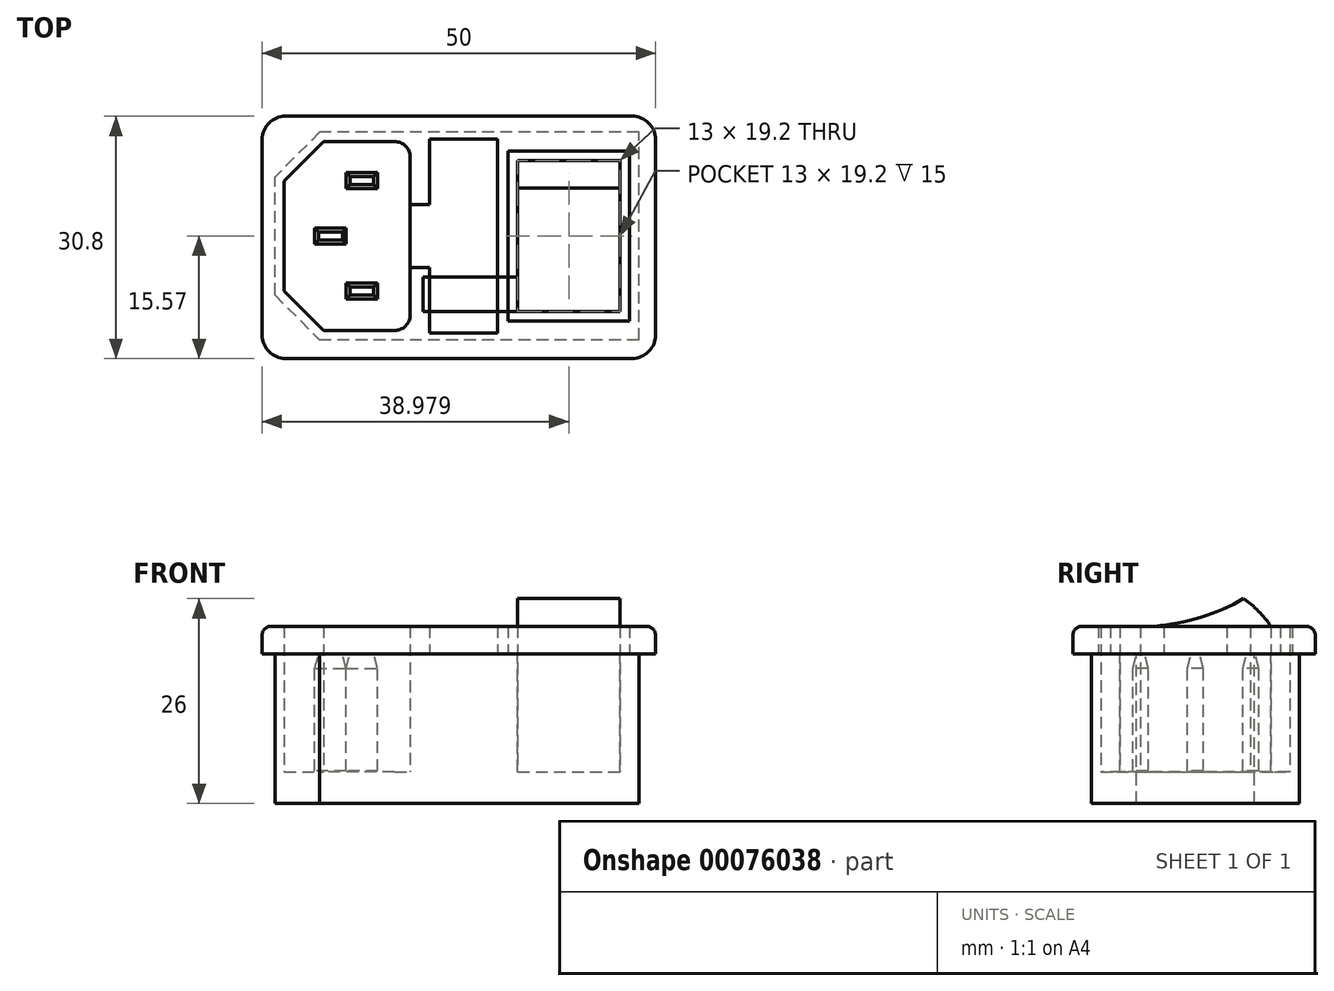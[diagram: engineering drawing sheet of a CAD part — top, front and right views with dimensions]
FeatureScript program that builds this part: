
annotation { "Feature Type Name" : "Feature", "Feature Type Description" : "" }
export const myFeature = defineFeature(function(context is Context, id is Id, definition is map)
    precondition{}
    {
        {
            var Q0;
            Q0=qCreatedBy(makeId("Top.planeOp"),FACE);
            var sketch = newSketch(context, id + "F0", { "sketchPlane" : qUnion([Q0])});
            skLineSegment(sketch, "E0.bottom", {"start": v(-22.59, 15.23) * mm, "end": v(21.41, 15.23) * mm});
            skLineSegment(sketch, "E0.top", {"start": v(-22.59, -15.57) * mm, "end": v(21.41, -15.57) * mm});
            skLineSegment(sketch, "E0.left", {"start": v(-25.59, 12.23) * mm, "end": v(-25.59, -12.57) * mm});
            skLineSegment(sketch, "E0.right", {"start": v(24.41, 12.23) * mm, "end": v(24.41, -12.57) * mm});
            skLineSegment(sketch, "E1.bottom", {"start": v(6.89, 9.6) * mm, "end": v(19.89, 9.6) * mm});
            skLineSegment(sketch, "E1.top", {"start": v(6.89, -9.6) * mm, "end": v(19.89, -9.6) * mm});
            skLineSegment(sketch, "E1.left", {"start": v(6.89, 9.6) * mm, "end": v(6.89, -9.6) * mm});
            skLineSegment(sketch, "E1.right", {"start": v(19.89, 9.6) * mm, "end": v(19.89, -9.6) * mm});
            skLineSegment(sketch, "E2.0", {"start": v(5.69, 10.8) * mm, "end": v(21.09, 10.8) * mm});
            skLineSegment(sketch, "E2.1", {"start": v(5.69, 10.8) * mm, "end": v(5.69, -10.8) * mm});
            skLineSegment(sketch, "E2.2", {"start": v(5.69, -10.8) * mm, "end": v(21.09, -10.8) * mm});
            skLineSegment(sketch, "E2.3", {"start": v(21.09, 10.8) * mm, "end": v(21.09, -10.8) * mm});
            skPoint(sketch, "E3", {"position": v(21.09, 0) * mm});
            skPoint(sketch, "E4", {"position": v(6.89, 0) * mm});
            skPoint(sketch, "E5", {"position": v(-0.59, -15.57) * mm});
            skPoint(sketch, "E6", {"position": v(-25.59, 0) * mm});
            skLineSegment(sketch, "E7.rect.bottom", {"start": v(-4.34, 12.33) * mm, "end": v(4.34, 12.33) * mm});
            skLineSegment(sketch, "E7.rect.top", {"start": v(-4.34, -12.33) * mm, "end": v(4.34, -12.33) * mm});
            skLineSegment(sketch, "E7.rect.left", {"start": v(-4.34, 12.33) * mm, "end": v(-4.34, -12.33) * mm});
            skLineSegment(sketch, "E7.rect.right", {"start": v(4.34, 12.33) * mm, "end": v(4.34, -12.33) * mm});
            skPoint(sketch, "E7.rect.middle", {"position": v(0, 0) * mm});
            skLineSegment(sketch, "E8.bottom", {"start": v(-8.76, -12) * mm, "end": v(-17.76, -12) * mm});
            skLineSegment(sketch, "E8.top", {"start": v(-8.76, 12) * mm, "end": v(-17.76, 12) * mm});
            skLineSegment(sketch, "E8.left", {"start": v(-6.76, -10) * mm, "end": v(-6.76, 10) * mm});
            skLineSegment(sketch, "E8.right", {"start": v(-22.76, -7) * mm, "end": v(-22.76, 7) * mm});
            skLineSegment(sketch, "E9", {"start": v(-17.76, 12) * mm, "end": v(-22.76, 7) * mm});
            skLineSegment(sketch, "E10", {"start": v(-22.76, -7) * mm, "end": v(-17.76, -12) * mm});
            skPoint(sketch, "E11", {"position": v(-6.76, 0) * mm});
            skPoint(sketch, "E12.visualSharp", {"position": v(24.41, 15.23) * mm});
            skArc(sketch, "E12.filletArc", {"start": v(24.41, 12.23) * mm, "mid": v(23.53, 14.35) * mm, "end": v(21.41, 15.23) * mm});
            skPoint(sketch, "E13.visualSharp", {"position": v(-25.59, 15.23) * mm});
            skArc(sketch, "E13.filletArc", {"start": v(-22.59, 15.23) * mm, "mid": v(-24.71, 14.35) * mm, "end": v(-25.59, 12.23) * mm});
            skPoint(sketch, "E14.visualSharp", {"position": v(-25.59, -15.57) * mm});
            skArc(sketch, "E14.filletArc", {"start": v(-25.59, -12.57) * mm, "mid": v(-24.71, -14.69) * mm, "end": v(-22.59, -15.57) * mm});
            skPoint(sketch, "E15.visualSharp", {"position": v(24.41, -15.57) * mm});
            skArc(sketch, "E15.filletArc", {"start": v(21.41, -15.57) * mm, "mid": v(23.53, -14.69) * mm, "end": v(24.41, -12.57) * mm});
            skPoint(sketch, "E16.visualSharp", {"position": v(-6.76, 12) * mm});
            skArc(sketch, "E16.filletArc", {"start": v(-6.76, 10) * mm, "mid": v(-7.34, 11.41) * mm, "end": v(-8.76, 12) * mm});
            skPoint(sketch, "E17.visualSharp", {"position": v(-6.76, -12) * mm});
            skArc(sketch, "E17.filletArc", {"start": v(-8.76, -12) * mm, "mid": v(-7.34, -11.41) * mm, "end": v(-6.76, -10) * mm});
            skLineSegment(sketch, "E18.rect.bottom", {"start": v(-14.89, 1) * mm, "end": v(-18.89, 1) * mm});
            skLineSegment(sketch, "E18.rect.top", {"start": v(-14.89, -1) * mm, "end": v(-18.89, -1) * mm});
            skLineSegment(sketch, "E18.rect.left", {"start": v(-14.89, 1) * mm, "end": v(-14.89, -1) * mm});
            skLineSegment(sketch, "E18.rect.right", {"start": v(-18.89, 1) * mm, "end": v(-18.89, -1) * mm});
            skPoint(sketch, "E18.rect.middle", {"position": v(-16.89, 0) * mm});
            skPoint(sketch, "E18.rect.middle.positionSnap0", {"position": v(-4.34, 0) * mm});
            skPoint(sketch, "E18.rect.centerSnap0", {"position": v(-4.34, 0) * mm});
            skLineSegment(sketch, "E19.rect.bottom", {"start": v(-10.89, 8.05) * mm, "end": v(-14.89, 8.05) * mm});
            skLineSegment(sketch, "E19.rect.right", {"start": v(-14.89, 8.05) * mm, "end": v(-14.89, 6.05) * mm});
            skLineSegment(sketch, "E19.rect.top", {"start": v(-10.89, 6.05) * mm, "end": v(-14.89, 6.05) * mm});
            skLineSegment(sketch, "E19.rect.left", {"start": v(-10.89, 8.05) * mm, "end": v(-10.89, 6.05) * mm});
            skPoint(sketch, "E19.rect.middle", {"position": v(-12.89, 7.05) * mm});
            skLineSegment(sketch, "E20.rect.bottom", {"start": v(-10.89, -5.97) * mm, "end": v(-14.89, -5.97) * mm});
            skLineSegment(sketch, "E20.rect.right", {"start": v(-14.89, -5.97) * mm, "end": v(-14.89, -7.97) * mm});
            skLineSegment(sketch, "E20.rect.top", {"start": v(-10.89, -7.97) * mm, "end": v(-14.89, -7.97) * mm});
            skLineSegment(sketch, "E20.rect.left", {"start": v(-10.89, -5.97) * mm, "end": v(-10.89, -7.97) * mm});
            skPoint(sketch, "E20.rect.middle", {"position": v(-12.89, -6.97) * mm});
            skLineSegment(sketch, "E21", {"start": v(-19.34, -78.26) * mm, "end": v(-26.2, -78.26) * mm});
            skLineSegment(sketch, "E22", {"start": v(-20.2, -74.76) * mm, "end": v(-25.73, -74.76) * mm});
            skLineSegment(sketch, "E23", {"start": v(-19.89, -48.56) * mm, "end": v(-26.2, -48.56) * mm});
            skLineSegment(sketch, "E24.0", {"start": v(-8.76, 13.2) * mm, "end": v(-18.25, 13.2) * mm});
            skLineSegment(sketch, "E24.1", {"start": v(-8.76, -13.2) * mm, "end": v(-18.25, -13.2) * mm});
            skLineSegment(sketch, "E24.2", {"start": v(-23.96, -7.5) * mm, "end": v(-18.25, -13.2) * mm});
            skLineSegment(sketch, "E24.3", {"start": v(-23.96, -7.5) * mm, "end": v(-23.96, 7.5) * mm});
            skLineSegment(sketch, "E24.4", {"start": v(-18.25, 13.2) * mm, "end": v(-23.96, 7.5) * mm});
            skLineSegment(sketch, "E25", {"start": v(-8.76, -13.2) * mm, "end": v(22.29, -13.2) * mm});
            skLineSegment(sketch, "E26", {"start": v(22.29, -13.2) * mm, "end": v(22.29, 13.2) * mm});
            skLineSegment(sketch, "E27", {"start": v(22.29, 13.2) * mm, "end": v(-8.76, 13.2) * mm});
            skLineSegment(sketch, "E28", {"start": v(-6.76, 4) * mm, "end": v(-4.34, 4) * mm});
            skLineSegment(sketch, "E29", {"start": v(-6.76, -4) * mm, "end": v(-4.34, -4) * mm});
            skSolve(sketch);
        }
        {
            var Q0;
            Q0=makeQuery(id+"F0.imprint","IMPRINT",FACE,{"disambiguationData":[TD([[makeQuery(id+"F0.imprint","IMPRINT",EDGE,{"derivedFrom":sQuery(id+"F0.wireOp",EDGE,"E0.bottom")}),-1.0]])]});
            var Q1;
            Q1=makeQuery(id+"F0.imprint","IMPRINT",FACE,{"disambiguationData":[TD([[makeQuery(id+"F0.imprint","IMPRINT",EDGE,{"derivedFrom":sQuery(id+"F0.wireOp",EDGE,"E2.0")}),1.0]])]});
            extrude(context, id + "F1", {"entities" : qUnion([Q0, Q1]), "depth" : 3.5 * mm});
        }
        {
            var Q0;
            Q0=makeQuery(id+"F0.imprint","IMPRINT",FACE,{"disambiguationData":[TD([[makeQuery(id+"F0.imprint","IMPRINT",EDGE,{"derivedFrom":sQuery(id+"F0.wireOp",EDGE,"E2.0")}),1.0]])]});
            var Q1;
            Q1=makeQuery(id+"F0.imprint","IMPRINT",FACE,{"disambiguationData":[TD([[makeQuery(id+"F0.imprint","IMPRINT",EDGE,{"derivedFrom":sQuery(id+"F0.wireOp",EDGE,"E8.bottom")}),-1.0]])]});
            var Q2;
            Q2=makeQuery(id+"F0.imprint","IMPRINT",FACE,{"disambiguationData":[TD([[makeQuery(id+"F0.imprint","IMPRINT",EDGE,{"derivedFrom":sQuery(id+"F0.wireOp",EDGE,"E1.bottom")}),-1.0]])]});
            var Q3;
            Q3=makeQuery(id+"F0.imprint","IMPRINT",FACE,{"disambiguationData":[TD([[makeQuery(id+"F0.imprint","IMPRINT",EDGE,{"derivedFrom":sQuery(id+"F0.wireOp",EDGE,"E1.bottom")}),1.0]])]});
            var Q4;
            Q4=makeQuery(id+"F0.imprint","IMPRINT",FACE,{"disambiguationData":[TD([[makeQuery(id+"F0.imprint","IMPRINT",EDGE,{"derivedFrom":sQuery(id+"F0.wireOp",EDGE,"E7.rect.bottom")}),-1.0]])]});
            var Q5;
            Q5=makeQuery(id+"F0.imprint","IMPRINT",FACE,{"disambiguationData":[TD([[makeQuery(id+"F0.imprint","IMPRINT",EDGE,{"derivedFrom":sQuery(id+"F0.wireOp",EDGE,"E20.rect.bottom")}),1.0]])]});
            var Q6;
            Q6=makeQuery(id+"F0.imprint","IMPRINT",FACE,{"disambiguationData":[TD([[makeQuery(id+"F0.imprint","IMPRINT",EDGE,{"derivedFrom":sQuery(id+"F0.wireOp",EDGE,"E18.rect.bottom")}),1.0]])]});
            var Q7;
            Q7=makeQuery(id+"F0.imprint","IMPRINT",FACE,{"disambiguationData":[TD([[makeQuery(id+"F0.imprint","IMPRINT",EDGE,{"derivedFrom":sQuery(id+"F0.wireOp",EDGE,"E19.rect.bottom")}),1.0]])]});
            var Q8;
            {var subQ0=sQuery(id+"F0.wireOp",EDGE,"E28");Q8=makeQuery(id+"F0.imprint","IMPRINT",FACE,{"disambiguationData":[TD([[makeQuery(id+"F0.imprint","IMPRINT",EDGE,{"derivedFrom":subQ0}),-1.0]])]});}
            extrude(context, id + "F2", {"entities" : qUnion([Q0, Q1, Q2, Q3, Q4, Q5, Q6, Q7, Q8]), "operationType" : NewBodyOperationType.ADD, "oppositeDirection" : true, "depth" : 19 * mm});
        }
        {
            var Q0;
            Q0=makeQuery(id+"F0.imprint","IMPRINT",FACE,{"disambiguationData":[TD([[makeQuery(id+"F0.imprint","IMPRINT",EDGE,{"derivedFrom":sQuery(id+"F0.wireOp",EDGE,"E8.bottom")}),-1.0]])]});
            var Q1;
            Q1=makeQuery(id+"F0.imprint","IMPRINT",FACE,{"disambiguationData":[TD([[makeQuery(id+"F0.imprint","IMPRINT",EDGE,{"derivedFrom":sQuery(id+"F0.wireOp",EDGE,"E1.bottom")}),-1.0]])]});
            extrude(context, id + "F3", {"entities" : qUnion([Q0, Q1]), "operationType" : NewBodyOperationType.REMOVE, "oppositeDirection" : true, "depth" : 15 * mm});
        }
        {
            var Q0;
            Q0=makeQuery(id+"F3.boolean.opBoolean","SPLIT",FACE,{"disambiguationData":[TD([makeQuery(id+"F3.opExtrude","SWEPT_FACE",FACE,{"disambiguationData":[OSD([sQuery(id+"F0.wireOp",EDGE,"E19.rect.bottom")])]})])],"derivedFrom":makeQuery(id+"F2.boolean.opBoolean","SPLIT",FACE,{"disambiguationData":[TD([makeQuery(id+"F1.opExtrude","SWEPT_FACE",FACE,{"disambiguationData":[OSD([sQuery(id+"F0.wireOp",EDGE,"E8.bottom")])]})])],"derivedFrom":makeQuery(id+"F2.opExtrude","CAP_FACE",FACE,{"disambiguationData":[OSD([sQuery(id+"F0.wireOp",EDGE,"E24.0"),sQuery(id+"F0.wireOp",EDGE,"E24.1"),sQuery(id+"F0.wireOp",EDGE,"E24.2"),sQuery(id+"F0.wireOp",EDGE,"E24.3"),sQuery(id+"F0.wireOp",EDGE,"E24.4"),sQuery(id+"F0.wireOp",EDGE,"E25"),sQuery(id+"F0.wireOp",EDGE,"E26"),sQuery(id+"F0.wireOp",EDGE,"E27")])],"isStart":true})})});
            chamfer(context, id + "F4", {"entities" : qUnion([Q0]), "chamferType" : ChamferType.OFFSET_ANGLE, "width" : 0.5 * mm, "oppositeDirection" : false, "angle" : 75 * degree, "tangentPropagation" : true});
        }
        {
            var Q0;
            Q0=makeQuery(id+"F3.boolean.opBoolean","SPLIT",FACE,{"disambiguationData":[TD([makeQuery(id+"F3.opExtrude","SWEPT_FACE",FACE,{"disambiguationData":[OSD([sQuery(id+"F0.wireOp",EDGE,"E18.rect.bottom")])]})])],"derivedFrom":makeQuery(id+"F2.boolean.opBoolean","SPLIT",FACE,{"disambiguationData":[TD([makeQuery(id+"F1.opExtrude","SWEPT_FACE",FACE,{"disambiguationData":[OSD([sQuery(id+"F0.wireOp",EDGE,"E8.bottom")])]})])],"derivedFrom":makeQuery(id+"F2.opExtrude","CAP_FACE",FACE,{"disambiguationData":[OSD([sQuery(id+"F0.wireOp",EDGE,"E24.0"),sQuery(id+"F0.wireOp",EDGE,"E24.1"),sQuery(id+"F0.wireOp",EDGE,"E24.2"),sQuery(id+"F0.wireOp",EDGE,"E24.3"),sQuery(id+"F0.wireOp",EDGE,"E24.4"),sQuery(id+"F0.wireOp",EDGE,"E25"),sQuery(id+"F0.wireOp",EDGE,"E26"),sQuery(id+"F0.wireOp",EDGE,"E27")])],"isStart":true})})});
            chamfer(context, id + "F5", {"entities" : qUnion([Q0]), "chamferType" : ChamferType.OFFSET_ANGLE, "width" : .5 * mm, "oppositeDirection" : false, "angle" : 75 * degree, "tangentPropagation" : true});
        }
        {
            var Q0;
            Q0=makeQuery(id+"F3.boolean.opBoolean","SPLIT",FACE,{"disambiguationData":[TD([makeQuery(id+"F3.opExtrude","SWEPT_FACE",FACE,{"disambiguationData":[OSD([sQuery(id+"F0.wireOp",EDGE,"E20.rect.bottom")])]})])],"derivedFrom":makeQuery(id+"F2.boolean.opBoolean","SPLIT",FACE,{"disambiguationData":[TD([makeQuery(id+"F1.opExtrude","SWEPT_FACE",FACE,{"disambiguationData":[OSD([sQuery(id+"F0.wireOp",EDGE,"E8.bottom")])]})])],"derivedFrom":makeQuery(id+"F2.opExtrude","CAP_FACE",FACE,{"disambiguationData":[OSD([sQuery(id+"F0.wireOp",EDGE,"E24.0"),sQuery(id+"F0.wireOp",EDGE,"E24.1"),sQuery(id+"F0.wireOp",EDGE,"E24.2"),sQuery(id+"F0.wireOp",EDGE,"E24.3"),sQuery(id+"F0.wireOp",EDGE,"E24.4"),sQuery(id+"F0.wireOp",EDGE,"E25"),sQuery(id+"F0.wireOp",EDGE,"E26"),sQuery(id+"F0.wireOp",EDGE,"E27")])],"isStart":true})})});
            chamfer(context, id + "F6", {"entities" : qUnion([Q0]), "chamferType" : ChamferType.OFFSET_ANGLE, "width" : .5 * mm, "oppositeDirection" : false, "angle" : 75 * degree, "tangentPropagation" : true});
        }
        {
            var Q0;
            {var subQ4=sQuery(id+"F0.wireOp",EDGE,"E7.rect.bottom");var subQ8=makeQuery(id+"F1.opExtrude","SWEPT_FACE",FACE,{"disambiguationData":[OSD([subQ4])]});Q0=makeQuery(id+"F3.boolean.opBoolean","SPLIT",FACE,{"disambiguationData":[TD([subQ8])],"derivedFrom":makeQuery(id+"F2.boolean.opBoolean","SPLIT",FACE,{"disambiguationData":[TD([subQ8])],"derivedFrom":makeQuery(id+"F2.opExtrude","CAP_FACE",FACE,{"disambiguationData":[OSD([sQuery(id+"F0.wireOp",EDGE,"E24.0"),sQuery(id+"F0.wireOp",EDGE,"E24.1"),sQuery(id+"F0.wireOp",EDGE,"E24.2"),sQuery(id+"F0.wireOp",EDGE,"E24.3"),sQuery(id+"F0.wireOp",EDGE,"E24.4"),sQuery(id+"F0.wireOp",EDGE,"E25"),sQuery(id+"F0.wireOp",EDGE,"E26"),sQuery(id+"F0.wireOp",EDGE,"E27")])],"isStart":true})})});}
            var Q1;
            Q1=makeQuery(id+"F2.boolean.opBoolean","SPLIT",FACE,{"disambiguationData":[TD([makeQuery(id+"F1.opExtrude","SWEPT_FACE",FACE,{"disambiguationData":[OSD([sQuery(id+"F0.wireOp",EDGE,"E2.0")])]})])],"derivedFrom":makeQuery(id+"F2.opExtrude","CAP_FACE",FACE,{"disambiguationData":[OSD([sQuery(id+"F0.wireOp",EDGE,"E24.0"),sQuery(id+"F0.wireOp",EDGE,"E24.1"),sQuery(id+"F0.wireOp",EDGE,"E24.2"),sQuery(id+"F0.wireOp",EDGE,"E24.3"),sQuery(id+"F0.wireOp",EDGE,"E24.4"),sQuery(id+"F0.wireOp",EDGE,"E25"),sQuery(id+"F0.wireOp",EDGE,"E26"),sQuery(id+"F0.wireOp",EDGE,"E27")])],"isStart":true})});
            var Q2;
            Q2=makeQuery(id+"F1.opExtrude","CAP_FACE",FACE,{"disambiguationData":[OSD([sQuery(id+"F0.wireOp",EDGE,"E0.bottom"),sQuery(id+"F0.wireOp",EDGE,"E0.top"),sQuery(id+"F0.wireOp",EDGE,"E0.left"),sQuery(id+"F0.wireOp",EDGE,"E0.right"),sQuery(id+"F0.wireOp",EDGE,"E2.0"),sQuery(id+"F0.wireOp",EDGE,"E2.1"),sQuery(id+"F0.wireOp",EDGE,"E2.2"),sQuery(id+"F0.wireOp",EDGE,"E2.3"),sQuery(id+"F0.wireOp",EDGE,"E7.rect.bottom"),sQuery(id+"F0.wireOp",EDGE,"E7.rect.top"),sQuery(id+"F0.wireOp",EDGE,"E7.rect.left"),sQuery(id+"F0.wireOp",EDGE,"E7.rect.right"),sQuery(id+"F0.wireOp",EDGE,"E8.bottom"),sQuery(id+"F0.wireOp",EDGE,"E8.top"),sQuery(id+"F0.wireOp",EDGE,"E8.left"),sQuery(id+"F0.wireOp",EDGE,"E8.right"),sQuery(id+"F0.wireOp",EDGE,"E9"),sQuery(id+"F0.wireOp",EDGE,"E10"),sQuery(id+"F0.wireOp",EDGE,"E12.filletArc"),sQuery(id+"F0.wireOp",EDGE,"E13.filletArc"),sQuery(id+"F0.wireOp",EDGE,"E14.filletArc"),sQuery(id+"F0.wireOp",EDGE,"E15.filletArc"),sQuery(id+"F0.wireOp",EDGE,"E16.filletArc"),sQuery(id+"F0.wireOp",EDGE,"E17.filletArc"),sQuery(id+"F0.wireOp",EDGE,"E28"),sQuery(id+"F0.wireOp",EDGE,"E29")])],"isStart":false});
            extrude(context, id + "F7", {"entities" : qUnion([Q0, Q1]), "endBound" : BoundingType.UP_TO_SURFACE, "endBoundEntityFace" : qUnion([Q2]), "depth" : 25 * mm});
        }
        {
            var Q0;
            Q0=makeQuery(id+"F3.boolean.opBoolean","COPY",FACE,{"derivedFrom":makeQuery(id+"F3.opExtrude","CAP_FACE",FACE,{"disambiguationData":[OSD([sQuery(id+"F0.wireOp",EDGE,"E1.bottom"),sQuery(id+"F0.wireOp",EDGE,"E1.top"),sQuery(id+"F0.wireOp",EDGE,"E1.left"),sQuery(id+"F0.wireOp",EDGE,"E1.right")])],"isStart":false})});
            extrude(context, id + "F8", {"entities" : qUnion([Q0]), "depth" : 22 * mm});
        }
        {
            var Q0;
            Q0=makeQuery(id+"F8.opExtrude","SWEPT_FACE",FACE,{"disambiguationData":[OSD([sQuery(id+"F0.wireOp",EDGE,"E1.right")])]});
            var sketch = newSketch(context, id + "F9", { "sketchPlane" : qUnion([Q0])});
            skLineSegment(sketch, "E30.0", {"start": v(12.23, 3.5) * mm, "end": v(-12.57, 3.5) * mm});
            skLineSegment(sketch, "E31.0", {"start": v(9.6, 7) * mm, "end": v(9.6, -15) * mm});
            skArc(sketch, "E32", {"start": v(9.6, 3.5) * mm, "mid": v(8.02, 5.4) * mm, "end": v(6.12, 7) * mm});
            skArc(sketch, "E33", {"start": v(-9.6, 3.5) * mm, "mid": v(-1.48, 4.06) * mm, "end": v(6.12, 7) * mm});
            skSolve(sketch);
        }
        {
            var Q0;
            {var subQ0=sQuery(id+"F9.wireOp",EDGE,"E33");var subQ1=sQuery(id+"F9.wireOp",EDGE,"E30.0");var subQ3=makeQuery(id+"F9.imprint","INTERSECT",VERTEX,{"derivedFrom":[subQ1,subQ0]});Q0=makeQuery(id+"F9.imprint","IMPRINT",FACE,{"disambiguationData":[TD([[makeQuery(id+"F9.imprint","IMPRINT",EDGE,{"disambiguationData":[TD([[subQ3,-1.0]])],"derivedFrom":subQ1}),1.0]])]});}
            var Q1;
            {var subQ0=sQuery(id+"F9.wireOp",EDGE,"E33");var subQ1=sQuery(id+"F9.wireOp",EDGE,"E30.0");var subQ5=makeQuery(id+"F9.imprint","INTERSECT",VERTEX,{"derivedFrom":[subQ1,subQ0]});Q1=makeQuery(id+"F9.imprint","IMPRINT",FACE,{"disambiguationData":[TD([[makeQuery(id+"F9.imprint","IMPRINT",EDGE,{"disambiguationData":[TD([[subQ5,-1.0]])],"derivedFrom":subQ0}),1.0]])]});}
            var Q2;
            {var subQ3=sQuery(id+"F9.wireOp",EDGE,"E32");Q2=makeQuery(id+"F9.imprint","IMPRINT",FACE,{"disambiguationData":[TD([[makeQuery(id+"F9.imprint","IMPRINT",EDGE,{"derivedFrom":subQ3}),-1.0]])]});}
            extrude(context, id + "F10", {"entities" : qUnion([Q0, Q1, Q2]), "operationType" : NewBodyOperationType.REMOVE, "oppositeDirection" : true, "depth" : 25 * mm});
        }
        {
            var Q0;
            Q0=makeQuery(id+"F1.opExtrude","CAP_EDGE",EDGE,{"disambiguationData":[OSD([sQuery(id+"F0.wireOp",EDGE,"E0.left")])],"isStart":false});
            fillet(context, id + "F11", {"entities" : qUnion([Q0]), "radius" : 1.2 * mm, "tangentPropagation" : true, "allowEdgeOverflow" : false});
        }
        {
            var Q0;
            Q0=makeQuery(id+"F0.imprint","IMPRINT",FACE,{"disambiguationData":[TD([[makeQuery(id+"F0.imprint","IMPRINT",EDGE,{"derivedFrom":sQuery(id+"F0.wireOp",EDGE,"E19.rect.bottom")}),1.0]])]});
            var Q1;
            Q1=makeQuery(id+"F0.imprint","IMPRINT",FACE,{"disambiguationData":[TD([[makeQuery(id+"F0.imprint","IMPRINT",EDGE,{"derivedFrom":sQuery(id+"F0.wireOp",EDGE,"E18.rect.bottom")}),1.0]])]});
            var Q2;
            Q2=makeQuery(id+"F0.imprint","IMPRINT",FACE,{"disambiguationData":[TD([[makeQuery(id+"F0.imprint","IMPRINT",EDGE,{"derivedFrom":sQuery(id+"F0.wireOp",EDGE,"E20.rect.bottom")}),1.0]])]});
            var Q3;
            Q3=makeQuery(id+"F3.boolean.opBoolean","COPY",FACE,{"derivedFrom":makeQuery(id+"F3.opExtrude","CAP_FACE",FACE,{"disambiguationData":[OSD([sQuery(id+"F0.wireOp",EDGE,"E8.bottom"),sQuery(id+"F0.wireOp",EDGE,"E8.top"),sQuery(id+"F0.wireOp",EDGE,"E8.left"),sQuery(id+"F0.wireOp",EDGE,"E8.right"),sQuery(id+"F0.wireOp",EDGE,"E9"),sQuery(id+"F0.wireOp",EDGE,"E10"),sQuery(id+"F0.wireOp",EDGE,"E16.filletArc"),sQuery(id+"F0.wireOp",EDGE,"E17.filletArc"),sQuery(id+"F0.wireOp",EDGE,"E18.rect.bottom"),sQuery(id+"F0.wireOp",EDGE,"E18.rect.top"),sQuery(id+"F0.wireOp",EDGE,"E18.rect.left"),sQuery(id+"F0.wireOp",EDGE,"E18.rect.right"),sQuery(id+"F0.wireOp",EDGE,"E19.rect.bottom"),sQuery(id+"F0.wireOp",EDGE,"E19.rect.right"),sQuery(id+"F0.wireOp",EDGE,"E19.rect.top"),sQuery(id+"F0.wireOp",EDGE,"E19.rect.left"),sQuery(id+"F0.wireOp",EDGE,"E20.rect.bottom"),sQuery(id+"F0.wireOp",EDGE,"E20.rect.right"),sQuery(id+"F0.wireOp",EDGE,"E20.rect.top"),sQuery(id+"F0.wireOp",EDGE,"E20.rect.left")])],"isStart":false})});
            extrude(context, id + "F12", {"entities" : qUnion([Q0, Q1, Q2]), "operationType" : NewBodyOperationType.REMOVE, "endBound" : BoundingType.UP_TO_SURFACE, "oppositeDirection" : true, "endBoundEntityFace" : qUnion([Q3]), "depth" : 25 * mm, "hasSecondDirection" : true, "secondDirectionOppositeDirection" : true, "secondDirectionDepth" : 14.9 * mm});
        }
    });
